# Revit family: Sanitary_Accessories_Johnson-Suisse_Cube_Towel_Ring_20x22cm
name_source: partatom
category: Plumbing Fixtures
revit_build: Autodesk Revit 2015 (Build: 20140606_1530(x64)
units: mm (PartAtom-declared; Revit-internal decimal feet)

## types (1)
- Cube Towel Ring 20x22cm
    BIMobject category = Accessories
    Brand url = http://www.johnsonsuisse.com.au
    Design country = Spain
    EAN code = https://9325304004556
    Edition number = 1
    IFC Classification = Furnishing Element
    Manufacturer country = China
    Manufacturer name = Johnson Suisse
    Material main = Metal
    Material secondary = Chrome
    NBS Reference Code = 35-75-91
    NBS Reference Description = Towel Rings
    Nominal height = 220 mm  [stored 0.721785 ft]
    Nominal width = 200 mm  [stored 0.656168 ft]
    Product Guid = 775b1860-c77a-426c-be4c-60744b46384b
    Product SKU = GDC160172
    Product data url = https://bimobject.com
    Product family = Cube
    Product group = Accessories
    Product url = https://johnsonsuisse.com.au
    QR code = http://bimobject.com
    Technical description = https://johnsonsuisse.com.au
    Type = cube_towel_ring_20x22cm : Default
    UNSPSC Code = 301815
    Uniclass 1.4 Code = L824
    Uniclass 1.4 Description = Bathroom, toilet furniture and fittings
    Uniclass 2.0 Code = PR-35-75-91
    Uniclass 2.0 Description = Towel Rings
    Uniclass 2015 Code = Pr_40_20_76_91
    Uniclass 2015 Name = Towel rings
    Weight Net (Kg) = 0.319

note: [stored X ft] marks values corroborated as IEEE doubles in the binary element streams (Revit-internal decimal feet)

## geometry (parser evidence)
native form markers: Sweep x4
no freeform markers — native parametric forms only
